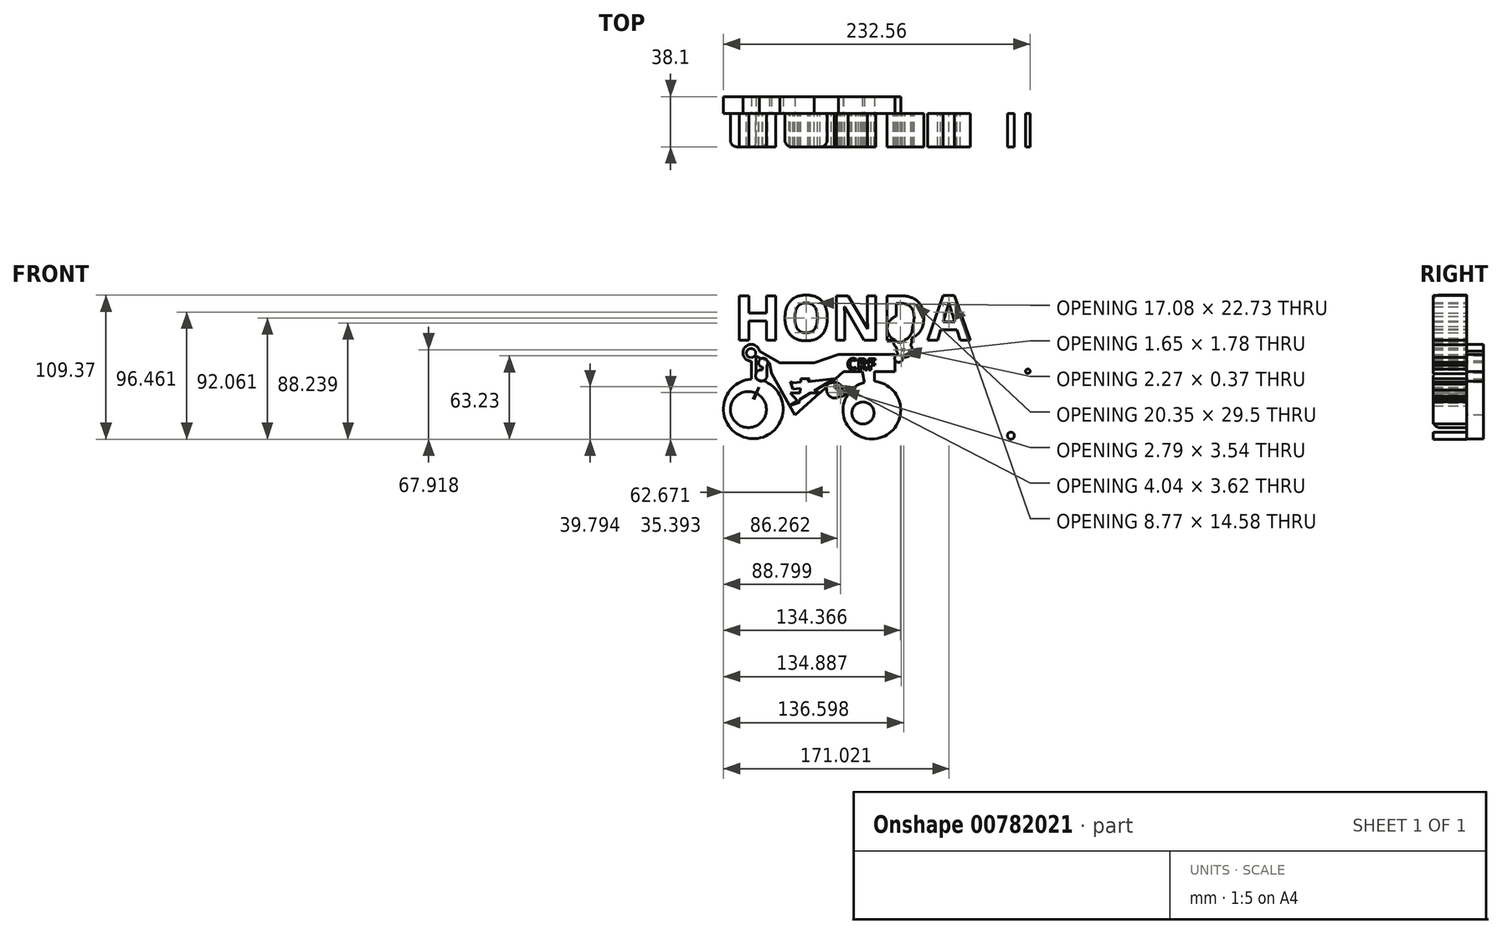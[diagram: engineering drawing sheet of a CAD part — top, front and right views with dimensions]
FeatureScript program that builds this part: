
annotation { "Feature Type Name" : "Feature", "Feature Type Description" : "" }
export const myFeature = defineFeature(function(context is Context, id is Id, definition is map)
    precondition{}
    {
        {
            var Q0;
            Q0=qCreatedBy(makeId("Front.planeOp"),FACE);
            var sketch = newSketch(context, id + "F0", { "sketchPlane" : qUnion([Q0])});
            skArc(sketch, "E0", {"start": v(-55.4, -12.46) * mm, "mid": v(-53.97, -57.66) * mm, "end": v(-51.92, -12.48) * mm});
            skCircle(sketch, "E1", {"center": v(36.14, -35.98) * mm, "radius": 21.88 * mm});
            skLineSegment(sketch, "E2", {"start": v(-39.93, -7.9) * mm, "end": v(-22.25, -39.77) * mm});
            skLineSegment(sketch, "E3", {"start": v(-22.25, -39.77) * mm, "end": v(14.68, -6.63) * mm});
            skLineSegment(sketch, "E4", {"start": v(14.68, -6.63) * mm, "end": v(53.5, -6.63) * mm});
            skLineSegment(sketch, "E5", {"start": v(53.5, -6.63) * mm, "end": v(53.5, 6.31) * mm});
            skLineSegment(sketch, "E6", {"start": v(53.5, 6.31) * mm, "end": v(10.89, 6.31) * mm});
            skLineSegment(sketch, "E7", {"start": v(10.89, 6.31) * mm, "end": v(-7.73, 0) * mm});
            skLineSegment(sketch, "E8", {"start": v(-7.73, 0) * mm, "end": v(-41.5, 0) * mm});
            skLineSegment(sketch, "E9", {"start": v(-41.5, 0) * mm, "end": v(-39.93, -7.9) * mm});
            skCircle(sketch, "E10", {"center": v(-55.4, 7.57) * mm, "radius": 6.34 * mm});
            skLineSegment(sketch, "E11.left", {"start": v(-55.4, 1.23) * mm, "end": v(-55.4, -12.46) * mm});
            skLineSegment(sketch, "E11.right", {"start": v(-51.92, 5.05) * mm, "end": v(-51.92, -12.48) * mm});
            skLineSegment(sketch, "E12", {"start": v(-49.2, 8.92) * mm, "end": v(-33.61, 0) * mm});
            skLineSegment(sketch, "E13", {"start": v(-33.61, 0) * mm, "end": v(-41.5, 0) * mm});
            skLineSegment(sketch, "E14", {"start": v(-41.5, 0) * mm, "end": v(-51.92, 5.05) * mm});
            skLineSegment(sketch, "E15", {"start": v(28.88, -6.63) * mm, "end": v(31.06, -17.55) * mm});
            skLineSegment(sketch, "E16", {"start": v(31.06, -17.55) * mm, "end": v(38.03, -17.55) * mm});
            skLineSegment(sketch, "E17", {"start": v(38.03, -17.55) * mm, "end": v(38.03, 0) * mm});
            skPoint(sketch, "E18.orphan", {"position": v(-55.4, 5.05) * mm});
            skSolve(sketch);
        }
        {
            var Q0;
            Q0=makeQuery(id+"F0.imprint","IMPRINT",FACE,{"disambiguationData":[TD([[makeQuery(id+"F0.imprint","IMPRINT",EDGE,{"derivedFrom":sQuery(id+"F0.wireOp",EDGE,"E2")}),1.0]])]});
            var Q1;
            {var subQ0=sQuery(id+"F0.wireOp",EDGE,"E12");Q1=makeQuery(id+"F0.imprint","IMPRINT",FACE,{"disambiguationData":[TD([[makeQuery(id+"F0.imprint","IMPRINT",EDGE,{"derivedFrom":subQ0}),-1.0]])]});}
            var Q2;
            {var subQ0=sQuery(id+"F0.wireOp",EDGE,"E10");var subQ4=makeQuery(id+"F0.imprint","INTERSECT",VERTEX,{"derivedFrom":[subQ0,sQuery(id+"F0.wireOp",EDGE,"E11.left")]});Q2=makeQuery(id+"F0.imprint","IMPRINT",FACE,{"disambiguationData":[TD([[makeQuery(id+"F0.imprint","IMPRINT",EDGE,{"disambiguationData":[TD([[subQ4,1.0]])],"derivedFrom":subQ0}),1.0]])]});}
            var Q3;
            {var subQ5=sQuery(id+"F0.wireOp",EDGE,"E16");Q3=makeQuery(id+"F0.imprint","IMPRINT",FACE,{"disambiguationData":[TD([[makeQuery(id+"F0.imprint","IMPRINT",EDGE,{"derivedFrom":subQ5}),-1.0]])]});}
            var Q4;
            {var subQ0=sQuery(id+"F0.wireOp",EDGE,"E15");var subQ1=sQuery(id+"F0.wireOp",EDGE,"E1");var subQ2=makeQuery(id+"F0.imprint","INTERSECT",VERTEX,{"derivedFrom":[subQ1,subQ0]});Q4=makeQuery(id+"F0.imprint","IMPRINT",FACE,{"disambiguationData":[TD([[makeQuery(id+"F0.imprint","IMPRINT",EDGE,{"disambiguationData":[TD([[subQ2,1.0]])],"derivedFrom":subQ1}),-1.0]])]});}
            var Q5;
            {var subQ5=sQuery(id+"F0.wireOp",EDGE,"E16");Q5=makeQuery(id+"F0.imprint","IMPRINT",FACE,{"disambiguationData":[TD([[makeQuery(id+"F0.imprint","IMPRINT",EDGE,{"derivedFrom":subQ5}),1.0]])]});}
            var Q6;
            {var subQ0=sQuery(id+"F0.wireOp",EDGE,"E0");Q6=makeQuery(id+"F0.imprint","IMPRINT",FACE,{"disambiguationData":[TD([[makeQuery(id+"F0.imprint","IMPRINT",EDGE,{"derivedFrom":subQ0}),1.0]])]});}
            extrude(context, id + "F1", {"entities" : qUnion([Q0, Q1, Q2, Q3, Q4, Q5, Q6]), "oppositeDirection" : true, "depth" : 12.7 * mm, "offsetDistance" : 25.4 * mm});
        }
        {
            var Q0;
            Q0=qCreatedBy(makeId("Front.planeOp"),FACE);
            var sketch = newSketch(context, id + "F2", { "sketchPlane" : qUnion([Q0])});
            skCircle(sketch, "E19", {"center": v(-55.52, 7.34) * mm, "radius": 3.47 * mm});
            skLineSegment(sketch, "E20", {"start": v(-26.74, -32.67) * mm, "end": v(-8.04, -26.33) * mm});
            skLineSegment(sketch, "E21", {"start": v(-3.14, -22.88) * mm, "end": v(-30.77, -22.88) * mm});
            skLineSegment(sketch, "E22", {"start": v(7.5, -12.23) * mm, "end": v(-26.74, -32.67) * mm});
            skLineSegment(sketch, "E23", {"start": v(-25.6, -22.88) * mm, "end": v(-16.96, -32.67) * mm});
            skPoint(sketch, "E23.endSnap0", {"position": v(-16.96, -22.88) * mm});
            skLineSegment(sketch, "E24", {"start": v(122.63, -55.4) * mm, "end": v(132.99, -58.28) * mm});
            skLineSegment(sketch, "E25", {"start": v(132.99, -58.28) * mm, "end": v(150.15, -52.47) * mm});
            skLineSegment(sketch, "E26", {"start": v(-26.74, -12.23) * mm, "end": v(-11.2, -12.23) * mm});
            skLineSegment(sketch, "E27", {"start": v(-26.46, -12.52) * mm, "end": v(-23.9, -20.1) * mm});
            skLineSegment(sketch, "E28", {"start": v(-11.2, -12.23) * mm, "end": v(-14.94, -18.85) * mm});
            skLineSegment(sketch, "E29", {"start": v(-14.94, -18.85) * mm, "end": v(-23.9, -20.1) * mm});
            skLineSegment(sketch, "E30", {"start": v(-38.54, -9.64) * mm, "end": v(-3.14, -22.88) * mm});
            skLineSegment(sketch, "E31", {"start": v(-35.67, -16.55) * mm, "end": v(7.5, -12.23) * mm});
            skLineSegment(sketch, "E32", {"start": v(-16.96, 0) * mm, "end": v(-19.42, -37.85) * mm});
            skPoint(sketch, "E32.endSnap0", {"position": v(-19.42, -19.48) * mm});
            skCircle(sketch, "E33", {"center": v(56.43, 3.3) * mm, "radius": 3 * mm});
            skCircle(sketch, "E34", {"center": v(60.46, 7.05) * mm, "radius": 3 * mm});
            skCircle(sketch, "E35", {"center": v(60.74, 10.04) * mm, "radius": 5.96 * mm});
            skCircle(sketch, "E36", {"center": v(57.3, 26.05) * mm, "radius": 9.57 * mm});
            skCircle(sketch, "E37", {"center": v(57.3, 20.3) * mm, "radius": 4.85 * mm});
            skCircle(sketch, "E38", {"center": v(59.4, 16.71) * mm, "radius": 7.03 * mm});
            skCircle(sketch, "E39", {"center": v(-57.54, -35.54) * mm, "radius": 13.68 * mm});
            skCircle(sketch, "E40", {"center": v(29.38, -38.13) * mm, "radius": 8.4 * mm});
            skLineSegment(sketch, "E41", {"start": v(-51.5, -23.28) * mm, "end": v(-47.75, -13.67) * mm});
            skLineSegment(sketch, "E42", {"start": v(-57.54, -35.54) * mm, "end": v(-37.68, -50.8) * mm});
            skLineSegment(sketch, "E43", {"start": v(-57.54, -35.54) * mm, "end": v(-30.77, -32.1) * mm});
            skLineSegment(sketch, "E44", {"start": v(-57.54, -35.54) * mm, "end": v(-49.62, -18.47) * mm});
            skLineSegment(sketch, "E45", {"start": v(-57.54, -35.54) * mm, "end": v(-73.52, -23.27) * mm});
            skLineSegment(sketch, "E46", {"start": v(-57.54, -35.54) * mm, "end": v(-72.8, -49.07) * mm});
            skLineSegment(sketch, "E47", {"start": v(-57.54, -35.54) * mm, "end": v(-54.8, -56.76) * mm});
            skLineSegment(sketch, "E48", {"start": v(29.38, -38.13) * mm, "end": v(50.1, -19.71) * mm});
            skLineSegment(sketch, "E49", {"start": v(29.38, -38.13) * mm, "end": v(54.9, -47.68) * mm});
            skLineSegment(sketch, "E50", {"start": v(29.38, -38.13) * mm, "end": v(29.38, -56.84) * mm});
            skLineSegment(sketch, "E51", {"start": v(29.38, -38.13) * mm, "end": v(15.74, -35.54) * mm});
            skLineSegment(sketch, "E52", {"start": v(29.38, -38.13) * mm, "end": v(24.49, -17.7) * mm});
            skLineSegment(sketch, "E53", {"start": v(3.76, -17.7) * mm, "end": v(16.33, -27.35) * mm});
            skLineSegment(sketch, "E54", {"start": v(4.84, -13.82) * mm, "end": v(17.1, -23.24) * mm});
            skLineSegment(sketch, "E55", {"start": v(-43.44, 0) * mm, "end": v(-43.44, -13.67) * mm});
            skLineSegment(sketch, "E56", {"start": v(-46.31, 0) * mm, "end": v(-47.75, -9.64) * mm});
            skCircle(sketch, "E57", {"center": v(-46.31, 0) * mm, "radius": 3.5 * mm});
            skCircle(sketch, "E58", {"center": v(4.84, -18.53) * mm, "radius": 3.27 * mm});
            skCircle(sketch, "E59", {"center": v(10.05, -17.82) * mm, "radius": 2.26 * mm});
            skPoint(sketch, "E59.centerSnap0", {"position": v(10.05, -22.53) * mm});
            skCircle(sketch, "E60", {"center": v(7.79, -20.79) * mm, "radius": 5.97 * mm});
            skCircle(sketch, "E61", {"center": v(13.26, -23.18) * mm, "radius": 2.3 * mm});
            skCircle(sketch, "E62", {"center": v(-47.75, -9.64) * mm, "radius": 4.32 * mm});
            skCircle(sketch, "E63", {"center": v(141.57, -55.38) * mm, "radius": 2.67 * mm});
            skCircle(sketch, "E64", {"center": v(154.42, -6.48) * mm, "radius": 1.7 * mm});
            skText(sketch, "E65", { "text": "CRF", "fontName": "OpenSans-Bold.ttf"});
            skText(sketch, "E66", { "text": "HONDA ", "fontName": "OpenSans-Bold.ttf"});
            const initialGuessF2  = {"E65": [0.01714, -0.00532, 1, 0, 0.00863], "E66": [-0.06863, 0.01712, 1, 0, 0.03396]};
            skSetInitialGuess(sketch, initialGuessF2);
            skSolve(sketch);
        }
        {
            var Q0;
            Q0 = qSketchRegion(id + "F2", true);
            extrude(context, id + "F3", {"entities" : qUnion([Q0]), "operationType" : NewBodyOperationType.ADD, "depth" : 25.4 * mm, "offsetDistance" : 25.4 * mm});
        }
        {
            var Q0;
            Q0=makeQuery(id+"F3.opExtrude","CAP_EDGE",EDGE,{"disambiguationData":[OSD([sQuery(id+"F2.wireOp",EDGE,"E66.sketch_text.stroke-15")])],"isStart":false});
            var Q1;
            Q1=makeQuery(id+"F3.opExtrude","CAP_EDGE",EDGE,{"disambiguationData":[OSD([sQuery(id+"F2.wireOp",EDGE,"E39")])],"isStart":false});
            fillet(context, id + "F4", {"entities" : qUnion([Q0, Q1]), "radius" : 5.08 * mm, "tangentPropagation" : true, "allowEdgeOverflow" : false});
        }
    });
